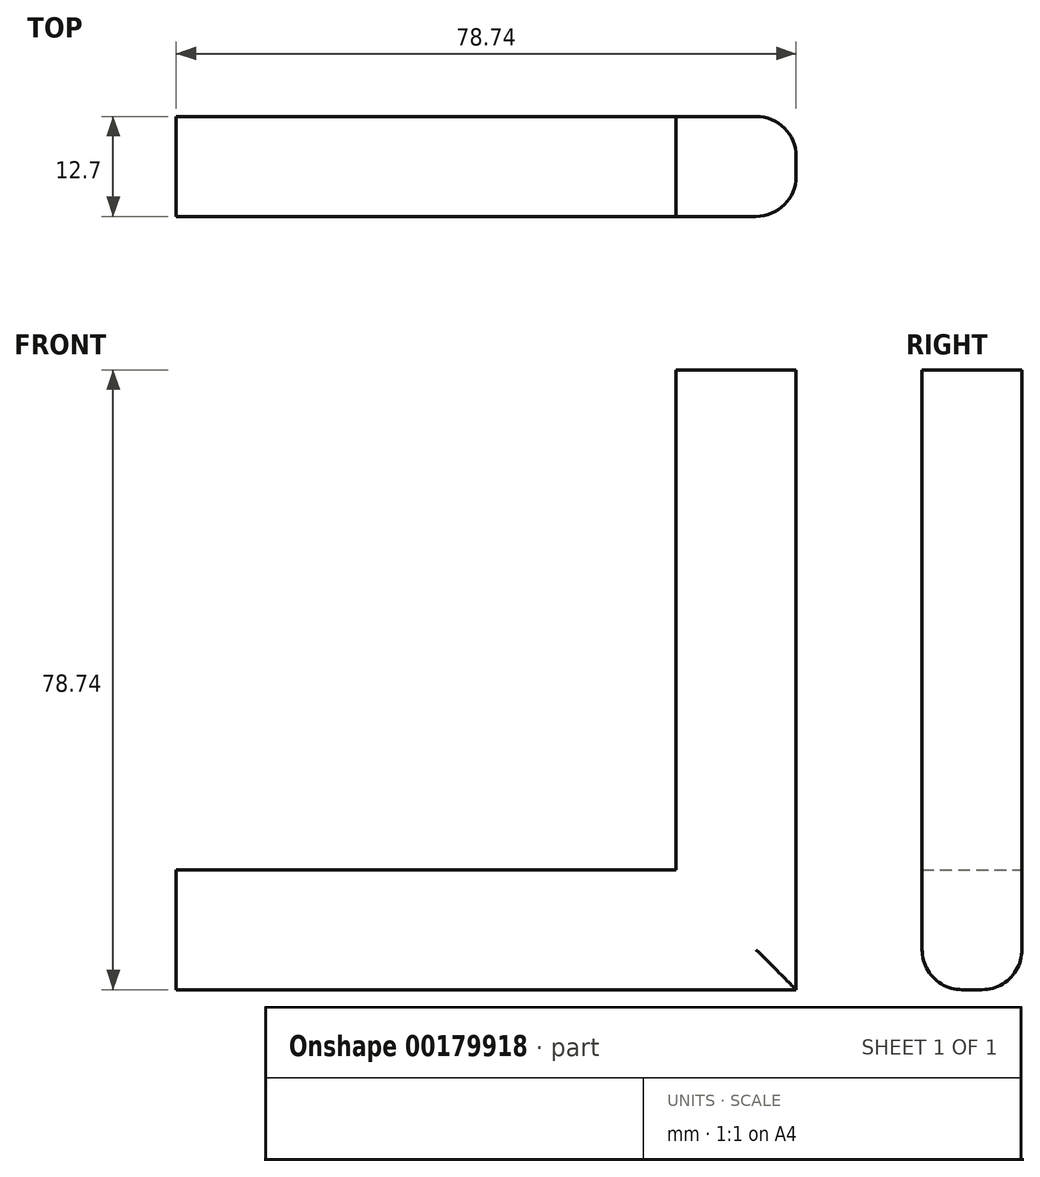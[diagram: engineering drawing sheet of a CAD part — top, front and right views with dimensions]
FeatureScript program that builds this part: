
annotation { "Feature Type Name" : "Feature", "Feature Type Description" : "" }
export const myFeature = defineFeature(function(context is Context, id is Id, definition is map)
    precondition{}
    {
        {
            var Q0;
            Q0=qCreatedBy(makeId("Front.planeOp"),FACE);
            var sketch = newSketch(context, id + "F0", { "sketchPlane" : qUnion([Q0])});
            skLineSegment(sketch, "E0", {"start": v(-63.5, 0) * mm, "end": v(0, 0) * mm});
            skLineSegment(sketch, "E1", {"start": v(0, 0) * mm, "end": v(0, 63.5) * mm});
            skLineSegment(sketch, "E2", {"start": v(0, 63.5) * mm, "end": v(15.24, 63.5) * mm});
            skLineSegment(sketch, "E3", {"start": v(15.24, 63.5) * mm, "end": v(15.24, -15.24) * mm});
            skLineSegment(sketch, "E4", {"start": v(15.24, -15.24) * mm, "end": v(-63.5, -15.24) * mm});
            skLineSegment(sketch, "E5", {"start": v(-63.5, 0) * mm, "end": v(-63.5, -15.24) * mm});
            skSolve(sketch);
        }
        {
            var Q0;
            Q0=makeQuery(id+"F0.imprint","IMPRINT",FACE,{"disambiguationData":[TD([[makeQuery(id+"F0.imprint","IMPRINT",EDGE,{"derivedFrom":sQuery(id+"F0.wireOp",EDGE,"E0")}),-1.0]])]});
            extrude(context, id + "F1", {"entities" : qUnion([Q0]), "depth" : 12.7 * mm});
        }
        {
            var Q0;
            Q0=makeQuery(id+"F1.opExtrude","CAP_EDGE",EDGE,{"disambiguationData":[OSD([sQuery(id+"F0.wireOp",EDGE,"E3")])],"isStart":false});
            var Q1;
            Q1=makeQuery(id+"F1.opExtrude","CAP_EDGE",EDGE,{"disambiguationData":[OSD([sQuery(id+"F0.wireOp",EDGE,"E4")])],"isStart":false});
            var Q2;
            Q2=makeQuery(id+"F1.opExtrude","CAP_EDGE",EDGE,{"disambiguationData":[OSD([sQuery(id+"F0.wireOp",EDGE,"E4")])],"isStart":true});
            var Q3;
            Q3=makeQuery(id+"F1.opExtrude","CAP_EDGE",EDGE,{"disambiguationData":[OSD([sQuery(id+"F0.wireOp",EDGE,"E3")])],"isStart":true});
            fillet(context, id + "F2", {"entities" : qUnion([Q0, Q1, Q2, Q3]), "radius" : 5.08 * mm, "tangentPropagation" : true, "allowEdgeOverflow" : false});
        }
    });
